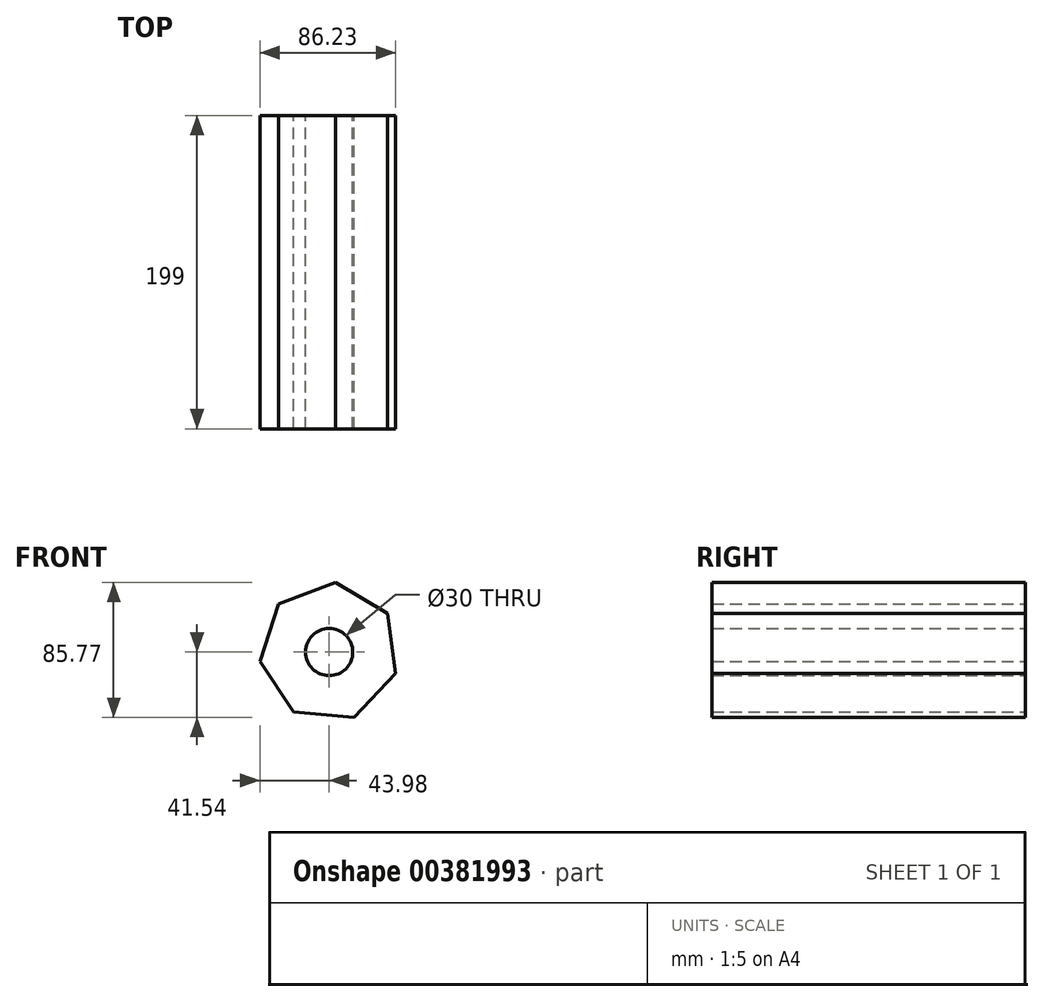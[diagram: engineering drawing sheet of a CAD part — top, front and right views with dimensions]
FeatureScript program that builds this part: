
annotation { "Feature Type Name" : "Feature", "Feature Type Description" : "" }
export const myFeature = defineFeature(function(context is Context, id is Id, definition is map)
    precondition{}
    {
        {
            var Q0;
            Q0=qCreatedBy(makeId("Front.planeOp"),FACE);
            var sketch = newSketch(context, id + "F0", { "sketchPlane" : qUnion([Q0])});
            skCircle(sketch, "E0.cCircle", {"center": v(0, 0) * mm, "radius": 40 * mm, "construction": true});
            skLineSegment(sketch, "E0.0", {"start": v(3.9, 44.23) * mm, "end": v(37, 24.53) * mm});
            skLineSegment(sketch, "E0.1", {"start": v(37, 24.53) * mm, "end": v(42.25, -13.64) * mm});
            skLineSegment(sketch, "E0.2", {"start": v(42.25, -13.64) * mm, "end": v(15.68, -41.54) * mm});
            skLineSegment(sketch, "E0.3", {"start": v(15.68, -41.54) * mm, "end": v(-22.7, -38.15) * mm});
            skLineSegment(sketch, "E0.4", {"start": v(-22.7, -38.15) * mm, "end": v(-43.98, -6.04) * mm});
            skLineSegment(sketch, "E0.5", {"start": v(-43.98, -6.04) * mm, "end": v(-32.15, 30.62) * mm});
            skLineSegment(sketch, "E0.6", {"start": v(-32.15, 30.62) * mm, "end": v(3.9, 44.23) * mm});
            skPoint(sketch, "E0.0.midPoint", {"position": v(20.45, 34.38) * mm});
            skSolve(sketch);
        }
        {
            var Q0;
            Q0 = qSketchRegion(id + "F0", true);
            extrude(context, id + "F1", {"entities" : qUnion([Q0]), "depth" : 199 * mm});
        }
        {
            var Q0;
            Q0=qCreatedBy(makeId("Front.planeOp"),FACE);
            var sketch = newSketch(context, id + "F2", { "sketchPlane" : qUnion([Q0])});
            skCircle(sketch, "E1", {"center": v(0, 0) * mm, "radius": 15 * mm});
            skSolve(sketch);
        }
        {
            var Q0;
            Q0 = qSketchRegion(id + "F2", true);
            extrude(context, id + "F3", {"entities" : qUnion([Q0]), "operationType" : NewBodyOperationType.REMOVE, "endBound" : BoundingType.THROUGH_ALL, "depth" : 25 * mm});
        }
    });
